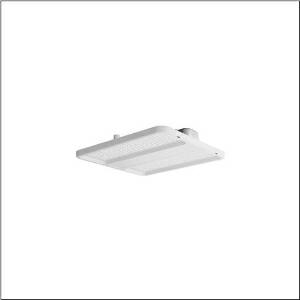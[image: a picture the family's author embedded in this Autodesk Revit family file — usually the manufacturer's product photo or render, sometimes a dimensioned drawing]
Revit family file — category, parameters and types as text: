
# Revit family: highbay_21_midi_52hn11da4nda
name_source: partatom
category: Lighting Fixtures
units: mm (PartAtom-declared; Revit-internal decimal feet)

## family parameters
Cut with Voids When Loaded = No
Host = Face
Light Source = No
Part Type = Normal
Room Calculation Point = No
Round Connector Dimension = Use Diameter
Shared = No

## types (1)
- --- (1 x LED, 5120 lm, 28.2 W, 4000K)
    Apparent Load = 28 VA
    CIE Flux Codes = 89 97 99 100 100
    Color Rendering = 80
    Color Temperature = 4000K
    Default Elevation = 1800 mm
    Description = high bay luminaire Highbay 21 midi; direct symmetric narrow distribution, light control with lens of PMMA; UGR ≤ 22 (X = 4H | Y = 8H | S = 0.25H | reflection values 70/50/20); luminous flux: 32.000lm; light colour: 840, colour temperature: 4000K, MacAdam ≤ 3 SDCM (initial), colour rendering: CRI > 80; luminous efficacy: 182lm/W; rated service life: 75.000h (L80/B50) at AT= ta max; control: DALI 2; housing frame of high-performance plastic PA6, matt traffic white (RAL 9016); cover of PMMA; dimension (LxWxH): 474 x 442 x 72mm; luminaire connection: terminal, 5-pole, max. 2.5mm² (cable entry for one cable, Ø 8.5..16mm); mains connection: 230..240V, AC/DC 0/50..60Hz; connected load: 175,8W; protection rating (complete): IP66; insulation class (complete): insulation class I (protective earthing); protection symbol: D; impact resistance: IK08; halogen-free wiring; for central battery installations according to DIN EN 60598-2-22; LABS conformity tested according to VDMA 24364:2018-05; corresponds to IFS (International Featured Standards) requirements for safety and quality in the food industry; certification: CE, ENEC, VDE, UKCA; permissible operating ambient temperature: -40..+50°C (reducing of maximum allowable ambient temperature of 5°C with ceiling mounting); packaging unit: 1 piece; (delivery without accessories; please order mounting accessories separately)
    Height = 72 mm  [stored 0.23622 ft]
    Lamp = 1 x LED
    Lamp Light Flux = 5120 lm
    Lamp Power = 28.2 W
    Lamp count = 1
    Length = 474 mm
    Luminous efficacy = 182 lm/W
    Manufacturer = Siteco
    ModVariant = No
    Model = 52HN11DA4NDA
    Mounting Place = Ceiling
    Mounting Type = Pendant
    Number of Poles = 1
    OnlyDefault = Yes
    Power Factor = 1
    Product Name = Highbay 21 midi
    Product group = high bay luminaire
    ProductGroupID = 901
    Protection Class = Protection class I
    Protection Degree = IP 66
    RLX_Detail_Level = 1
    RLX_Emergency_Light_Flux = 0 lm
    RLX_Emergency_Type = 0
    RLX_Emergency_Type_DB = No
    RlxData = <blob elided: 17681 chars, md5=b7977135>
    Socket = socket
    Standby Power = 0 W
    System Light Flux = 5120 lm
    System Power = 28 W
    Type Comments = : DC mode (central or group accumulator) initial emergency light level
    Type Image = l_1363240.jpg
    URL = http://relux.com
    VarID = @adj_000173
    Voltage = 0 V
    Weight = 0.00 kg
    Width = 442 mm

note: [stored X ft] marks values corroborated as IEEE doubles in the binary element streams (Revit-internal decimal feet)

## geometry (parser evidence)
native form markers: Blend x4, Sweep x12
no freeform markers — native parametric forms only
